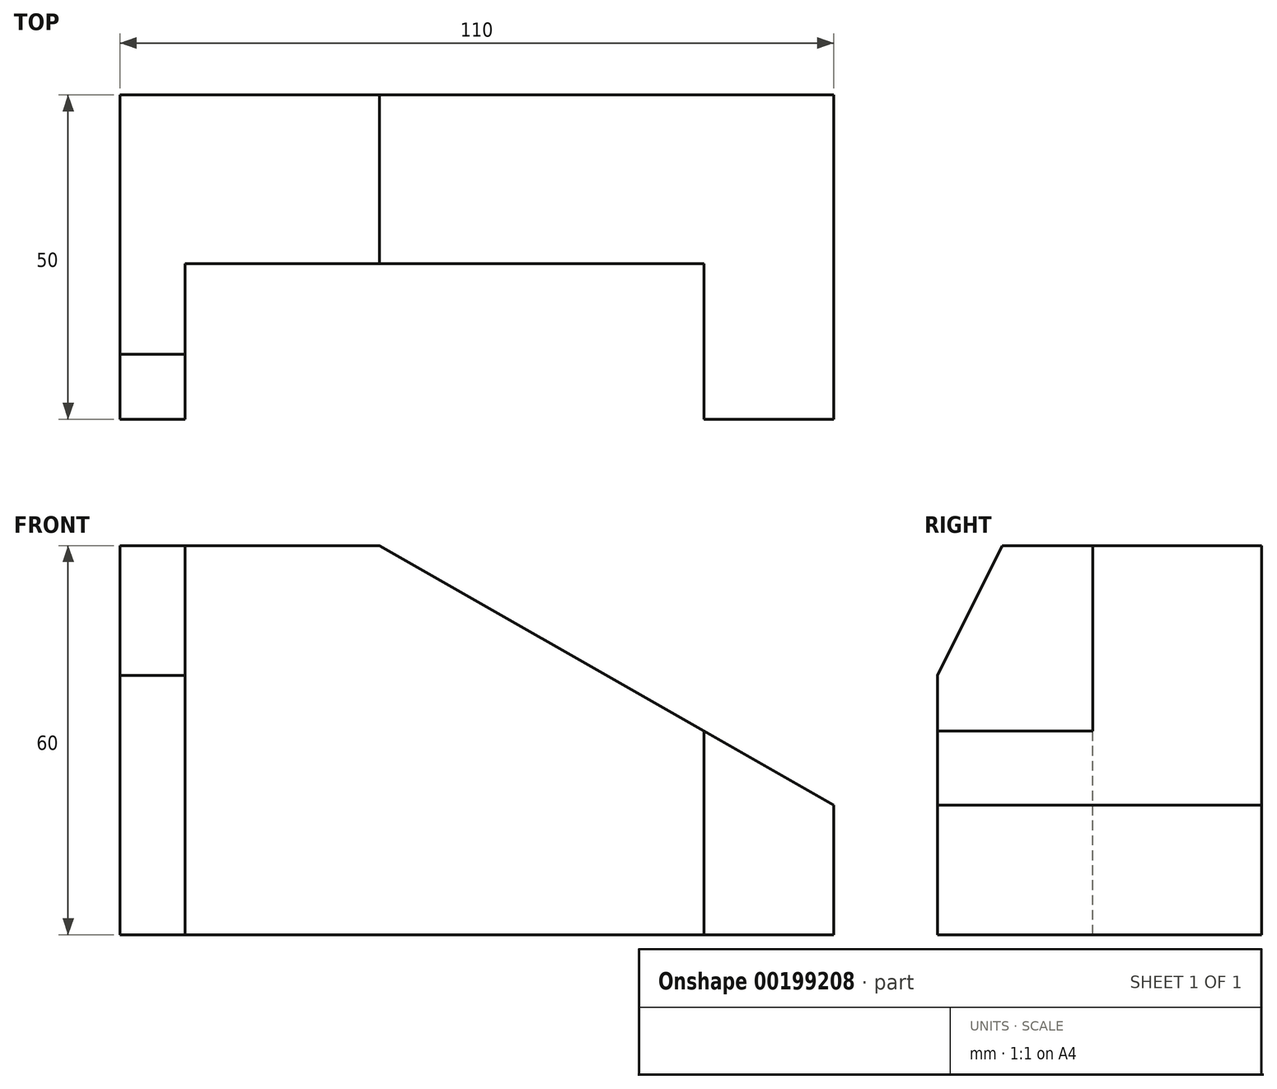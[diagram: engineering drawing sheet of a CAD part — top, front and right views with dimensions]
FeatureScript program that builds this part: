
annotation { "Feature Type Name" : "Feature", "Feature Type Description" : "" }
export const myFeature = defineFeature(function(context is Context, id is Id, definition is map)
    precondition{}
    {
        {
            var Q0;
            Q0=qCreatedBy(makeId("Front.planeOp"),FACE);
            var sketch = newSketch(context, id + "F0", { "sketchPlane" : qUnion([Q0])});
            skLineSegment(sketch, "E0", {"start": v(0, 0) * mm, "end": v(0, 20) * mm});
            skLineSegment(sketch, "E1", {"start": v(0, 0) * mm, "end": v(-110, 0) * mm});
            skLineSegment(sketch, "E2", {"start": v(-110, 0) * mm, "end": v(-110, 60) * mm});
            skLineSegment(sketch, "E3", {"start": v(-110, 60) * mm, "end": v(-70, 60) * mm});
            skLineSegment(sketch, "E4", {"start": v(-70, 60) * mm, "end": v(0, 20) * mm});
            skSolve(sketch);
        }
        {
            var Q0;
            Q0 = qSketchRegion(id + "F0", true);
            extrude(context, id + "F1", {"entities" : qUnion([Q0]), "oppositeDirection" : true, "depth" : 50 * mm});
        }
        {
            var Q0;
            Q0=makeQuery(id+"F1.opExtrude","SWEPT_FACE",FACE,{"disambiguationData":[OSD([sQuery(id+"F0.wireOp",EDGE,"E3")])]});
            var sketch = newSketch(context, id + "F2", { "sketchPlane" : qUnion([Q0])});
            skLineSegment(sketch, "E5", {"start": v(-100, 0) * mm, "end": v(-100, 23.96) * mm});
            skLineSegment(sketch, "E6", {"start": v(-100, 23.96) * mm, "end": v(-20, 23.96) * mm});
            skLineSegment(sketch, "E7", {"start": v(-20, 23.96) * mm, "end": v(-20, 0) * mm});
            skLineSegment(sketch, "E8", {"start": v(-20, 0) * mm, "end": v(-100, 0) * mm});
            skLineSegment(sketch, "E9", {"start": v(-110, 20) * mm, "end": v(-100, 20) * mm});
            skSolve(sketch);
        }
        {
            var Q0;
            {var subQ0=sQuery(id+"F2.wireOp",EDGE,"E5");Q0=makeQuery(id+"F2.imprint","IMPRINT",FACE,{"disambiguationData":[TD([[makeQuery(id+"F2.imprint","IMPRINT",EDGE,{"derivedFrom":subQ0}),-1.0]])]});}
            var Q1;
            {var subQ0=sQuery(id+"F2.wireOp",EDGE,"E7");Q1=makeQuery(id+"F2.imprint","IMPRINT",FACE,{"disambiguationData":[TD([[makeQuery(id+"F2.imprint","IMPRINT",EDGE,{"derivedFrom":subQ0}),-1.0]])]});}
            extrude(context, id + "F3", {"entities" : qUnion([Q0, Q1]), "operationType" : NewBodyOperationType.REMOVE, "endBound" : BoundingType.THROUGH_ALL, "oppositeDirection" : true, "depth" : 25 * mm});
        }
        {
            var Q0;
            Q0=makeQuery(id+"F1.opExtrude","CAP_EDGE",EDGE,{"disambiguationData":[OSD([sQuery(id+"F0.wireOp",EDGE,"E3")])],"isStart":true});
            chamfer(context, id + "F4", {"entities" : qUnion([Q0]), "chamferType" : ChamferType.TWO_OFFSETS, "width1" : 20 * mm, "oppositeDirection" : false, "width2" : 10 * mm, "tangentPropagation" : true});
        }
    });
